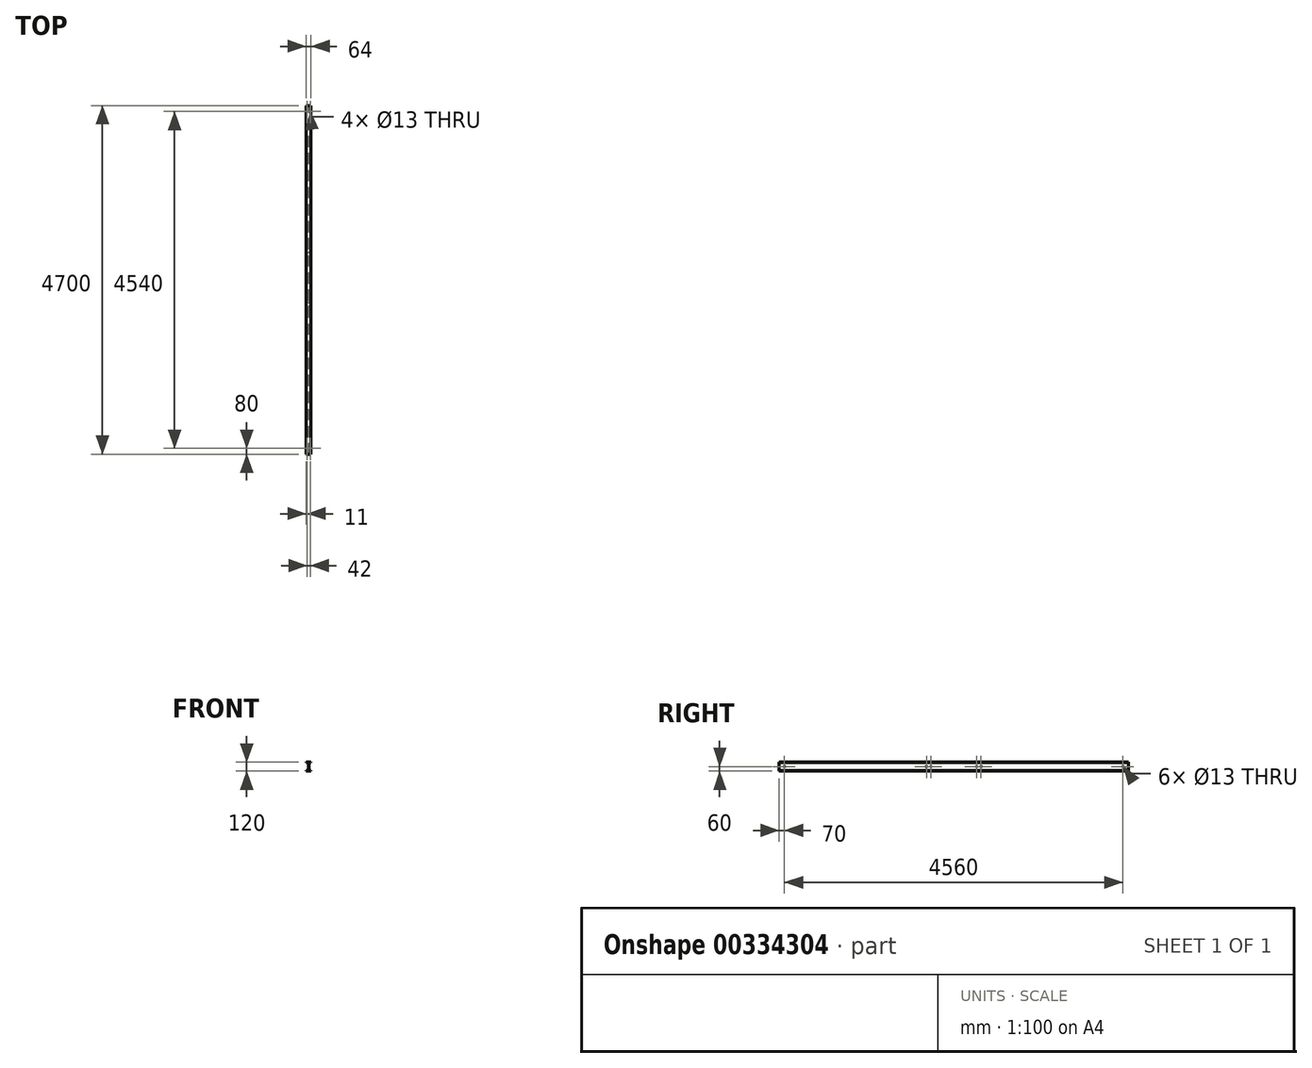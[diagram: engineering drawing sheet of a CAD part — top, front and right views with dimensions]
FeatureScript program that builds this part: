
annotation { "Feature Type Name" : "Feature", "Feature Type Description" : "" }
export const myFeature = defineFeature(function(context is Context, id is Id, definition is map)
    precondition{}
    {
        {
            var Q0;
            Q0=qCreatedBy(makeId("Front.planeOp"),FACE);
            var sketch = newSketch(context, id + "F0", { "sketchPlane" : qUnion([Q0])});
            skLineSegment(sketch, "E0", {"start": v(-32, 0) * mm, "end": v(32, 0) * mm});
            skLineSegment(sketch, "E1", {"start": v(32, 0) * mm, "end": v(32, 6.3) * mm});
            skLineSegment(sketch, "E2", {"start": v(32, 6.3) * mm, "end": v(9.2, 6.3) * mm});
            skLineSegment(sketch, "E3", {"start": v(2.2, 13.3) * mm, "end": v(2.2, 106.7) * mm});
            skLineSegment(sketch, "E4", {"start": v(9.2, 113.7) * mm, "end": v(32, 113.7) * mm});
            skLineSegment(sketch, "E5", {"start": v(32, 113.7) * mm, "end": v(32, 120) * mm});
            skLineSegment(sketch, "E6", {"start": v(32, 120) * mm, "end": v(-32, 120) * mm});
            skLineSegment(sketch, "E7", {"start": v(-32, 120) * mm, "end": v(-32, 113.7) * mm});
            skLineSegment(sketch, "E8", {"start": v(-32, 113.7) * mm, "end": v(-9.2, 113.7) * mm});
            skLineSegment(sketch, "E9", {"start": v(-2.2, 106.7) * mm, "end": v(-2.2, 13.3) * mm});
            skLineSegment(sketch, "E10", {"start": v(-9.2, 6.3) * mm, "end": v(-32, 6.3) * mm});
            skLineSegment(sketch, "E11", {"start": v(-32, 6.3) * mm, "end": v(-32, 0) * mm});
            skLineSegment(sketch, "E12", {"start": v(0, 0) * mm, "end": v(0, 0) * mm});
            skPoint(sketch, "E13.visualSharp", {"position": v(-2.2, 113.7) * mm});
            skArc(sketch, "E13.filletArc", {"start": v(-2.2, 106.7) * mm, "mid": v(-4.25, 111.65) * mm, "end": v(-9.2, 113.7) * mm});
            skPoint(sketch, "E14.visualSharp", {"position": v(-2.2, 6.3) * mm});
            skArc(sketch, "E14.filletArc", {"start": v(-9.2, 6.3) * mm, "mid": v(-4.25, 8.35) * mm, "end": v(-2.2, 13.3) * mm});
            skPoint(sketch, "E15.visualSharp", {"position": v(2.2, 6.3) * mm});
            skArc(sketch, "E15.filletArc", {"start": v(2.2, 13.3) * mm, "mid": v(4.25, 8.35) * mm, "end": v(9.2, 6.3) * mm});
            skPoint(sketch, "E16.visualSharp", {"position": v(2.2, 113.7) * mm});
            skArc(sketch, "E16.filletArc", {"start": v(9.2, 113.7) * mm, "mid": v(4.25, 111.65) * mm, "end": v(2.2, 106.7) * mm});
            skSolve(sketch);
        }
        {
            assignVariable(context, id + "F1", {"name" : "L_Pro", "anyValue" : 4700});
        }
        {
            var Q0;
            Q0=makeQuery(id+"F0.imprint","IMPRINT",FACE,{"disambiguationData":[TD([[makeQuery(id+"F0.imprint","IMPRINT",EDGE,{"derivedFrom":sQuery(id+"F0.wireOp",EDGE,"E0")}),1.0]])]});
            extrude(context, id + "F2", {"entities" : qUnion([Q0]), "depth" : (getVariable(context, 'L_Pro')) * mm});
        }
        {
            var Q0;
            Q0=makeQuery(id+"F2.opExtrude","SWEPT_FACE",FACE,{"disambiguationData":[OSD([sQuery(id+"F0.wireOp",EDGE,"E0")])]});
            var sketch = newSketch(context, id + "F3", { "sketchPlane" : qUnion([Q0])});
            skLineSegment(sketch, "E17", {"start": v(0, 4700) * mm, "end": v(0, 4620) * mm, "construction": true});
            skLineSegment(sketch, "E18", {"start": v(21, 4620) * mm, "end": v(-21, 4620) * mm, "construction": true});
            skLineSegment(sketch, "E19", {"start": v(21, 80) * mm, "end": v(-21, 80) * mm, "construction": true});
            skCircle(sketch, "E20", {"center": v(21, 80) * mm, "radius": 6.5 * mm});
            skCircle(sketch, "E21", {"center": v(-21, 80) * mm, "radius": 6.5 * mm});
            skCircle(sketch, "E22", {"center": v(21, 4620) * mm, "radius": 6.5 * mm});
            skCircle(sketch, "E23", {"center": v(-21, 4620) * mm, "radius": 6.5 * mm});
            skLineSegment(sketch, "E24.trimOffspring", {"start": v(0, 80) * mm, "end": v(0, 0) * mm, "construction": true});
            skSolve(sketch);
        }
        {
            var Q0;
            Q0=qSketchRegion(id+"F3",true);
            extrude(context, id + "F4", {"entities" : qUnion([Q0]), "operationType" : NewBodyOperationType.REMOVE, "endBound" : BoundingType.UP_TO_NEXT, "oppositeDirection" : true, "depth" : 25 * mm});
        }
        {
            var Q0;
            Q0=makeQuery(id+"F2.opExtrude","SWEPT_FACE",FACE,{"disambiguationData":[OSD([sQuery(id+"F0.wireOp",EDGE,"E9")])]});
            var sketch = newSketch(context, id + "F5", { "sketchPlane" : qUnion([Q0])});
            skLineSegment(sketch, "E25", {"start": v(0, 60) * mm, "end": v(70, 60) * mm, "construction": true});
            skCircle(sketch, "E26", {"center": v(70, 60) * mm, "radius": 6.5 * mm});
            skLineSegment(sketch, "E27", {"start": v(4700, 60) * mm, "end": v(4630, 60) * mm, "construction": true});
            skCircle(sketch, "E28", {"center": v(4630, 60) * mm, "radius": 6.5 * mm});
            skCircle(sketch, "E29", {"center": v(1982.5, 60) * mm, "radius": 6.5 * mm});
            skCircle(sketch, "E30", {"center": v(2042.5, 60) * mm, "radius": 6.5 * mm});
            skCircle(sketch, "E31", {"center": v(2717.5, 60) * mm, "radius": 6.5 * mm});
            skCircle(sketch, "E32", {"center": v(2657.5, 60) * mm, "radius": 6.5 * mm});
            skSolve(sketch);
        }
        {
            var Q0;
            Q0=qSketchRegion(id+"F5",true);
            extrude(context, id + "F6", {"entities" : qUnion([Q0]), "operationType" : NewBodyOperationType.REMOVE, "endBound" : BoundingType.THROUGH_ALL, "oppositeDirection" : true, "depth" : 25 * mm});
        }
    });
